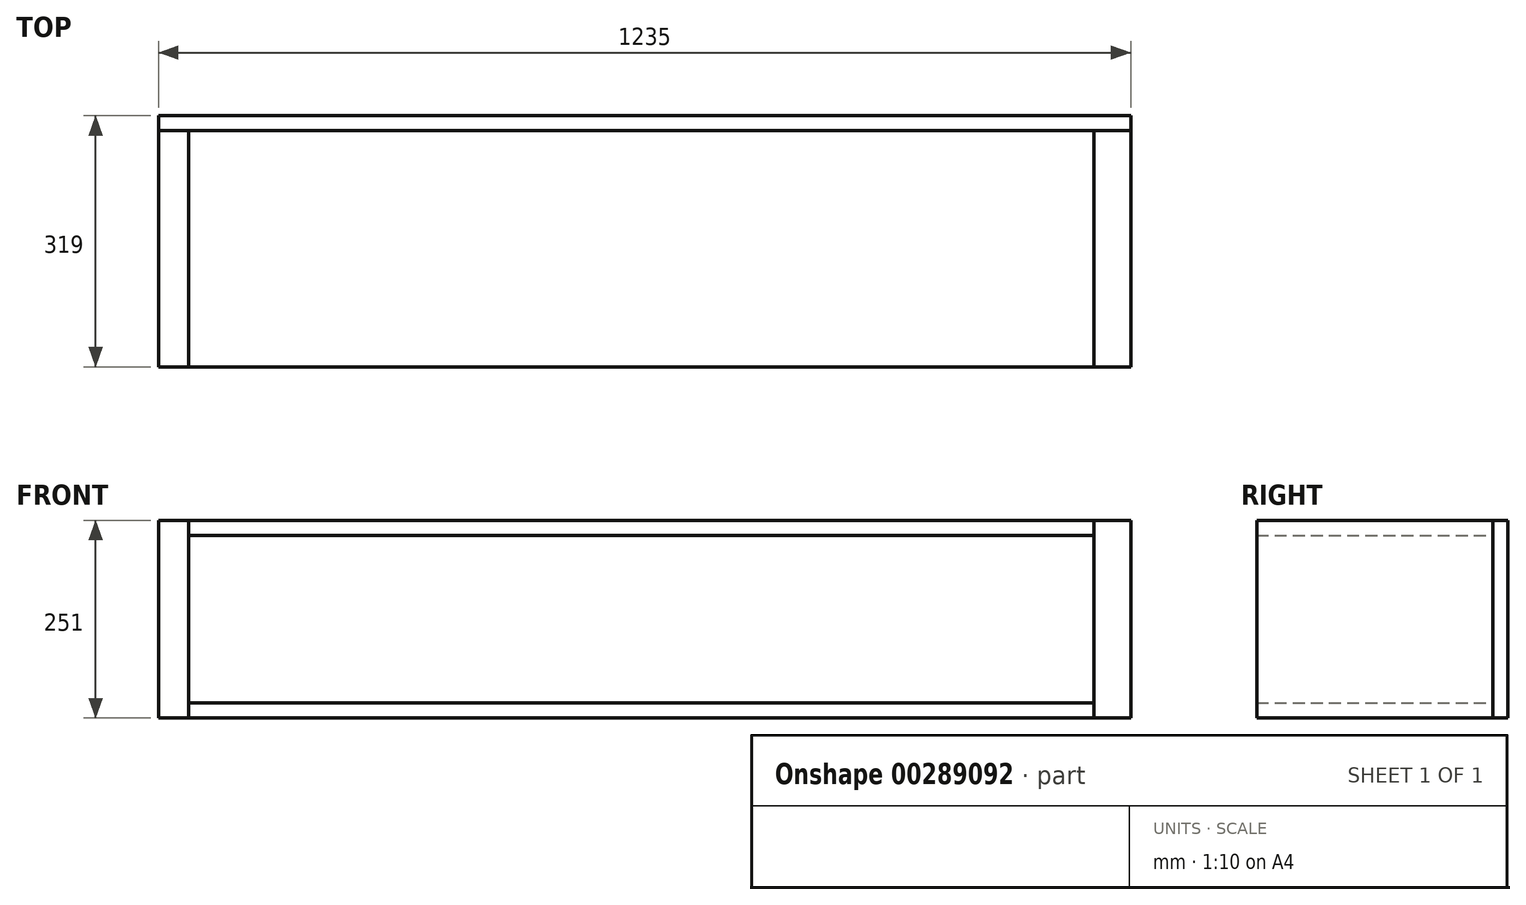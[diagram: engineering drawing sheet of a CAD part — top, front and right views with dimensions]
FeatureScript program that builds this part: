
annotation { "Feature Type Name" : "Feature", "Feature Type Description" : "" }
export const myFeature = defineFeature(function(context is Context, id is Id, definition is map)
    precondition{}
    {
        {
            var Q0;
            Q0=qCreatedBy(makeId("Front.planeOp"),FACE);
            var sketch = newSketch(context, id + "F0", { "sketchPlane" : qUnion([Q0])});
            skLineSegment(sketch, "E0.bottom", {"start": v(-615.31, 125.5) * mm, "end": v(619.69, 125.5) * mm});
            skLineSegment(sketch, "E0.left", {"start": v(-615.31, 125.5) * mm, "end": v(-615.31, -125.5) * mm});
            skLineSegment(sketch, "E0.right", {"start": v(619.69, 125.5) * mm, "end": v(619.69, -125.5) * mm});
            skLineSegment(sketch, "E1.bottom", {"start": v(-577.31, 106.5) * mm, "end": v(572.94, 106.5) * mm});
            skLineSegment(sketch, "E1.top", {"start": v(-577.31, -106.5) * mm, "end": v(572.94, -106.5) * mm});
            skLineSegment(sketch, "E1.left", {"start": v(-577.31, 106.5) * mm, "end": v(-577.31, -106.5) * mm});
            skLineSegment(sketch, "E1.right", {"start": v(572.94, 106.5) * mm, "end": v(572.94, -106.5) * mm});
            skLineSegment(sketch, "E2", {"start": v(619.69, -125.5) * mm, "end": v(-615.31, -125.5) * mm});
            skSolve(sketch);
        }
        {
            var Q0;
            Q0=qCreatedBy(makeId("Front.planeOp"),FACE);
            var sketch = newSketch(context, id + "F1", { "sketchPlane" : qUnion([Q0])});
            skLineSegment(sketch, "E3.bottom", {"start": v(-615.31, 125.5) * mm, "end": v(-577.31, 125.5) * mm});
            skLineSegment(sketch, "E3.top", {"start": v(-615.31, -125.5) * mm, "end": v(-577.31, -125.5) * mm});
            skLineSegment(sketch, "E3.left", {"start": v(-615.31, 125.5) * mm, "end": v(-615.31, -125.5) * mm});
            skLineSegment(sketch, "E3.right", {"start": v(-577.31, 125.5) * mm, "end": v(-577.31, -125.5) * mm});
            skLineSegment(sketch, "E4", {"start": v(0, 124.26) * mm, "end": v(0, 0) * mm, "construction": true});
            skLineSegment(sketch, "E5.bottom", {"start": v(572.94, -125.5) * mm, "end": v(619.69, -125.5) * mm});
            skLineSegment(sketch, "E5.top", {"start": v(572.94, 125.5) * mm, "end": v(619.69, 125.5) * mm});
            skLineSegment(sketch, "E5.left", {"start": v(572.94, -125.5) * mm, "end": v(572.94, 125.5) * mm});
            skLineSegment(sketch, "E5.right", {"start": v(619.69, -125.5) * mm, "end": v(619.69, 125.5) * mm});
            skSolve(sketch);
        }
        {
            var Q0;
            Q0=qSketchRegion(id+"F1",true);
            extrude(context, id + "F2", {"entities" : qUnion([Q0]), "depth" : 300 * mm});
        }
        {
            var Q0;
            Q0=qCreatedBy(makeId("Front.planeOp"),FACE);
            var sketch = newSketch(context, id + "F3", { "sketchPlane" : qUnion([Q0])});
            skLineSegment(sketch, "E6.bottom", {"start": v(-577.31, 125.5) * mm, "end": v(572.94, 125.5) * mm});
            skLineSegment(sketch, "E6.top", {"start": v(-577.31, 106.5) * mm, "end": v(572.94, 106.5) * mm});
            skLineSegment(sketch, "E6.left", {"start": v(-577.31, 125.5) * mm, "end": v(-577.31, 106.5) * mm});
            skLineSegment(sketch, "E6.right", {"start": v(572.94, 125.5) * mm, "end": v(572.94, 106.5) * mm});
            skLineSegment(sketch, "E7", {"start": v(0, 0) * mm, "end": v(572.48, 0) * mm, "construction": true});
            skLineSegment(sketch, "E8.MirrorCS", {"start": v(572.94, -125.5) * mm, "end": v(572.94, -106.5) * mm});
            skLineSegment(sketch, "E9.MirrorCS", {"start": v(-577.31, -125.5) * mm, "end": v(-577.31, -106.5) * mm});
            skLineSegment(sketch, "E10.MirrorCS", {"start": v(-577.31, -125.5) * mm, "end": v(572.94, -125.5) * mm});
            skLineSegment(sketch, "E11.MirrorCS", {"start": v(-577.31, -106.5) * mm, "end": v(572.94, -106.5) * mm});
            skSolve(sketch);
        }
        {
            var Q0;
            Q0=qSketchRegion(id+"F3",true);
            var Q1;
            Q1=makeQuery(id+"F2.opExtrude","CAP_FACE",FACE,{"disambiguationData":[OSD([sQuery(id+"F1.wireOp",EDGE,"E3.bottom"),sQuery(id+"F1.wireOp",EDGE,"E3.top"),sQuery(id+"F1.wireOp",EDGE,"E3.left"),sQuery(id+"F1.wireOp",EDGE,"E3.right")])],"isStart":false});
            extrude(context, id + "F4", {"entities" : qUnion([Q0]), "endBound" : BoundingType.UP_TO_SURFACE, "endBoundEntityFace" : qUnion([Q1]), "depth" : 25 * mm});
        }
        {
            var Q0;
            Q0=makeQuery(id+"F0.imprint","IMPRINT",FACE,{"disambiguationData":[TD([[makeQuery(id+"F0.imprint","IMPRINT",EDGE,{"derivedFrom":sQuery(id+"F0.wireOp",EDGE,"E0.bottom")}),-1.0]])]});
            var sketch = newSketch(context, id + "F5", { "sketchPlane" : qUnion([Q0])});
            skLineSegment(sketch, "E12.bottom", {"start": v(619.69, 125.5) * mm, "end": v(-615.31, 125.5) * mm});
            skLineSegment(sketch, "E12.top", {"start": v(619.69, -125.5) * mm, "end": v(-615.31, -125.5) * mm});
            skLineSegment(sketch, "E12.left", {"start": v(619.69, 125.5) * mm, "end": v(619.69, -125.5) * mm});
            skLineSegment(sketch, "E12.right", {"start": v(-615.31, 125.5) * mm, "end": v(-615.31, -125.5) * mm});
            skSolve(sketch);
        }
        {
            var Q0;
            Q0=qSketchRegion(id+"F5",true);
            extrude(context, id + "F6", {"entities" : qUnion([Q0]), "oppositeDirection" : true, "depth" : 19 * mm});
        }
    });
